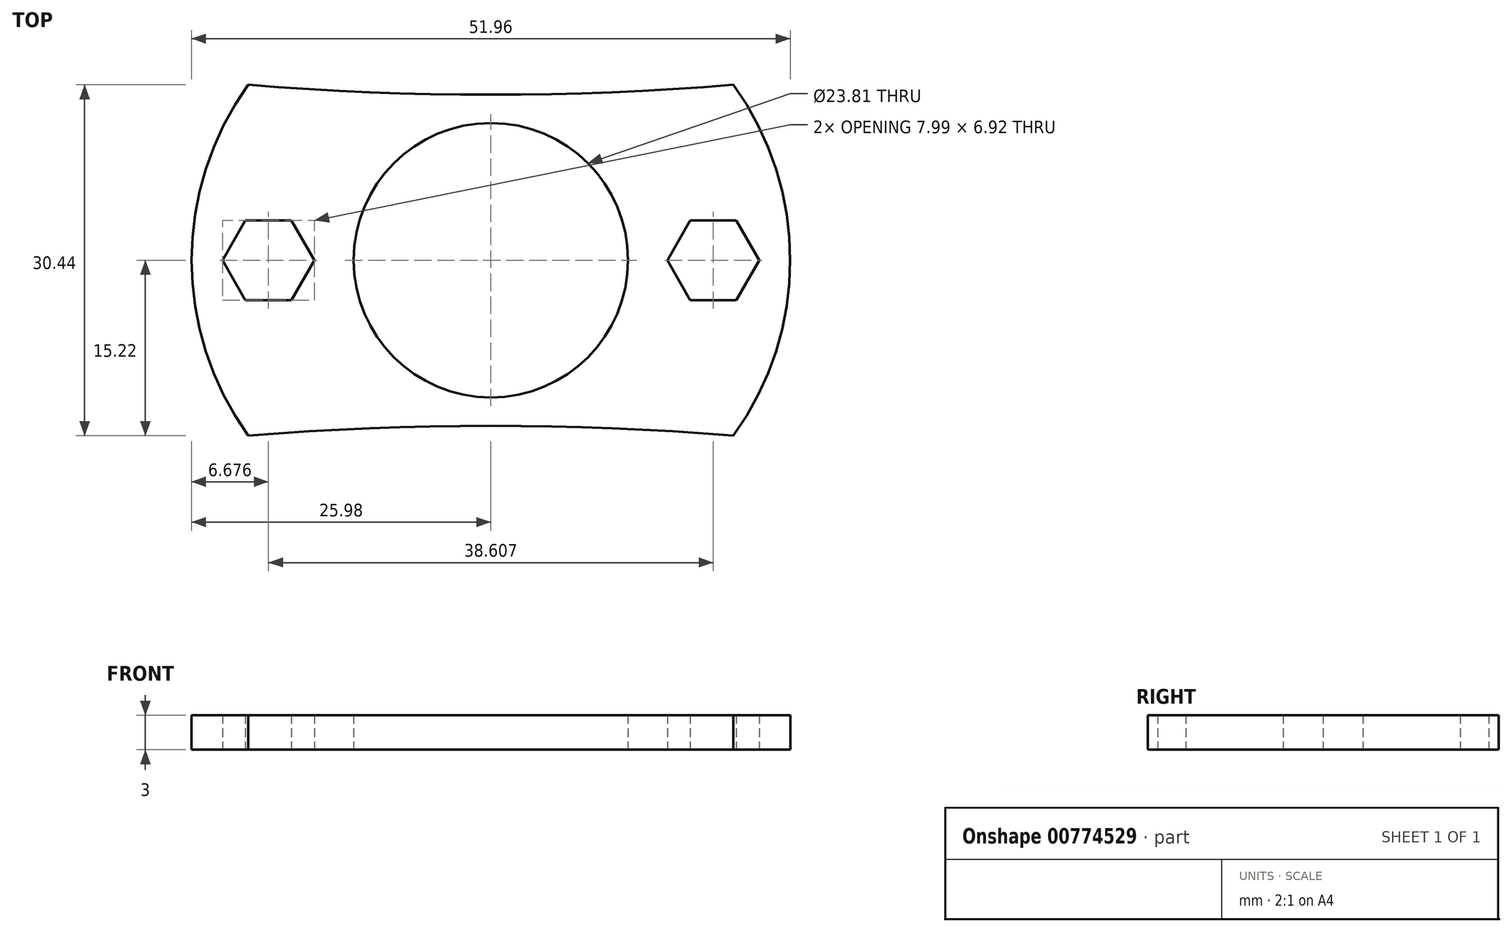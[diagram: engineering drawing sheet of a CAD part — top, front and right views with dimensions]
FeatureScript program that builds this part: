
annotation { "Feature Type Name" : "Feature", "Feature Type Description" : "" }
export const myFeature = defineFeature(function(context is Context, id is Id, definition is map)
    precondition{}
    {
        {
            var Q0;
            Q0=qCreatedBy(makeId("Top.planeOp"),FACE);
            var sketch = newSketch(context, id + "F0", { "sketchPlane" : qUnion([Q0])});
            skArc(sketch, "E0", {"start": v(11.9, 0) * mm, "mid": v(8.42, 8.42) * mm, "end": v(0, 11.9) * mm});
            skArc(sketch, "E1", {"start": v(25.98, 0) * mm, "mid": v(24.71, 8) * mm, "end": v(21.05, 15.22) * mm});
            skArc(sketch, "E2.MirrorCS", {"start": v(-11.9, 0) * mm, "mid": v(-8.42, 8.42) * mm, "end": v(0, 11.9) * mm});
            skArc(sketch, "E3.MirrorCS", {"start": v(-25.98, 0) * mm, "mid": v(-24.71, 8) * mm, "end": v(-21.05, 15.22) * mm});
            skPoint(sketch, "E4.MirrorCS.end.orphan", {"position": v(-21.05, 15.22) * mm});
            skPoint(sketch, "E4.MirrorCS.start.orphan", {"position": v(0, 14.36) * mm});
            skArc(sketch, "E5", {"start": v(-21.05, 15.22) * mm, "mid": v(0, 14.36) * mm, "end": v(21.05, 15.22) * mm});
            skArc(sketch, "E6.MirrorCS", {"start": v(11.9, 0) * mm, "mid": v(8.42, -8.42) * mm, "end": v(0, -11.9) * mm});
            skPoint(sketch, "E7.MirrorP", {"position": v(0, -14.36) * mm});
            skArc(sketch, "E8.MirrorCS", {"start": v(-11.9, 0) * mm, "mid": v(-8.42, -8.42) * mm, "end": v(0, -11.9) * mm});
            skArc(sketch, "E9.MirrorCS", {"start": v(25.98, 0) * mm, "mid": v(24.71, -8) * mm, "end": v(21.05, -15.22) * mm});
            skArc(sketch, "E10.MirrorCS", {"start": v(-21.05, -15.22) * mm, "mid": v(0, -14.36) * mm, "end": v(21.05, -15.22) * mm});
            skPoint(sketch, "E11.MirrorP", {"position": v(-21.05, -15.22) * mm});
            skArc(sketch, "E12.MirrorCS", {"start": v(-25.98, 0) * mm, "mid": v(-24.71, -8) * mm, "end": v(-21.05, -15.22) * mm});
            skCircle(sketch, "E13.cCircle", {"center": v(-19.3, 0) * mm, "radius": 3.46 * mm, "construction": true});
            skLineSegment(sketch, "E13.0", {"start": v(-15.3, 0) * mm, "end": v(-17.3, -3.46) * mm});
            skLineSegment(sketch, "E13.1", {"start": v(-17.3, -3.46) * mm, "end": v(-21.3, -3.46) * mm});
            skLineSegment(sketch, "E13.2", {"start": v(-21.3, -3.46) * mm, "end": v(-23.3, 0) * mm});
            skLineSegment(sketch, "E13.3", {"start": v(-23.3, 0) * mm, "end": v(-21.3, 3.46) * mm});
            skLineSegment(sketch, "E13.4", {"start": v(-21.3, 3.46) * mm, "end": v(-17.3, 3.46) * mm});
            skLineSegment(sketch, "E13.5", {"start": v(-17.3, 3.46) * mm, "end": v(-15.3, 0) * mm});
            skPoint(sketch, "E13.0.midPoint", {"position": v(-16.3, -1.73) * mm});
            skLineSegment(sketch, "E14.MirrorCS", {"start": v(21.3, 3.46) * mm, "end": v(17.3, 3.46) * mm});
            skLineSegment(sketch, "E15.MirrorCS", {"start": v(21.3, -3.46) * mm, "end": v(23.3, 0) * mm});
            skLineSegment(sketch, "E16.MirrorCS", {"start": v(15.3, 0) * mm, "end": v(17.3, -3.46) * mm});
            skPoint(sketch, "E17.MirrorP", {"position": v(16.3, -1.73) * mm});
            skLineSegment(sketch, "E18.MirrorCS", {"start": v(17.3, 3.46) * mm, "end": v(15.3, 0) * mm});
            skCircle(sketch, "E19.MirrorC", {"center": v(19.3, 0) * mm, "radius": 3.46 * mm, "construction": true});
            skLineSegment(sketch, "E20.MirrorCS", {"start": v(23.3, 0) * mm, "end": v(21.3, 3.46) * mm});
            skLineSegment(sketch, "E21.MirrorCS", {"start": v(17.3, -3.46) * mm, "end": v(21.3, -3.46) * mm});
            skSolve(sketch);
        }
        {
            var Q0;
            Q0 = qSketchRegion(id + "F0", true);
            extrude(context, id + "F1", {"entities" : qUnion([Q0]), "depth" : 3 * mm, "offsetDistance" : 25 * mm});
        }
    });
